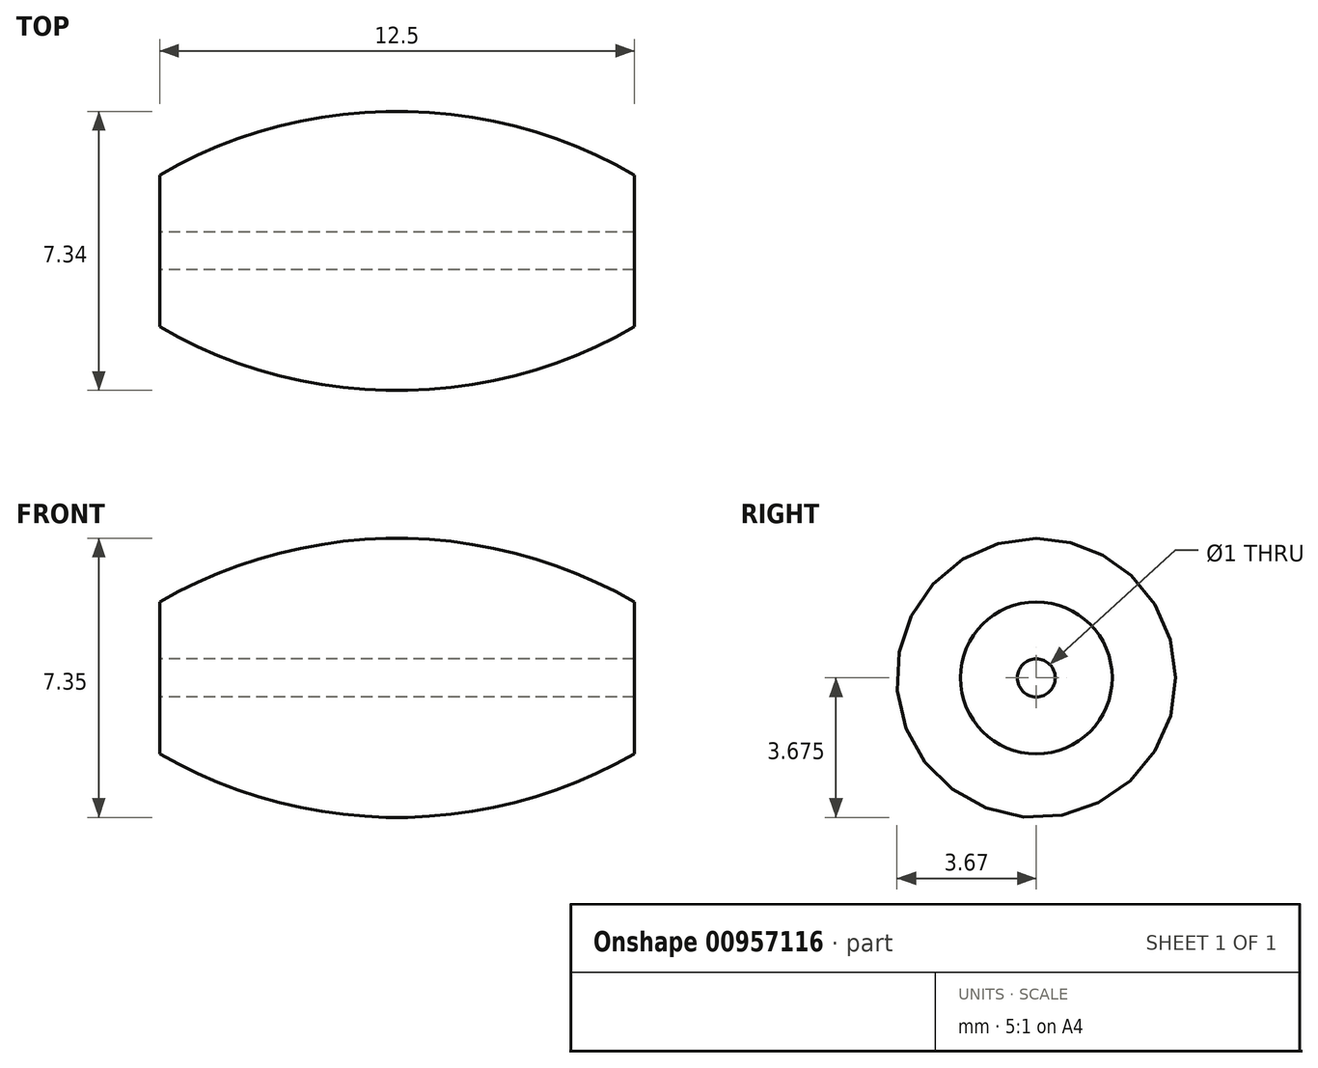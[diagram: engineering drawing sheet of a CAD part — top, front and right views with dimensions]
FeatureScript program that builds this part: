
annotation { "Feature Type Name" : "Feature", "Feature Type Description" : "" }
export const myFeature = defineFeature(function(context is Context, id is Id, definition is map)
    precondition{}
    {
        {
            var Q0;
            Q0=qCreatedBy(makeId("Front.planeOp"),FACE);
            var sketch = newSketch(context, id + "F0", { "sketchPlane" : qUnion([Q0])});
            skArc(sketch, "E0", {"start": v(6.25, 10.83) * mm, "mid": v(0, 12.5) * mm, "end": v(-6.25, 10.83) * mm});
            skLineSegment(sketch, "E1", {"start": v(0, 0) * mm, "end": v(0, 18.01) * mm, "construction": true});
            skLineSegment(sketch, "E2", {"start": v(0, 0) * mm, "end": v(-9.74, 16.86) * mm, "construction": true});
            skLineSegment(sketch, "E3", {"start": v(-6.25, 10.83) * mm, "end": v(-6.25, 9.33) * mm});
            skLineSegment(sketch, "E4", {"start": v(-6.25, 9.33) * mm, "end": v(0, 9.33) * mm});
            skLineSegment(sketch, "E5", {"start": v(-11.7, 8.83) * mm, "end": v(16.89, 8.83) * mm, "construction": true});
            skLineSegment(sketch, "E6.MirrorCS", {"start": v(0, 0) * mm, "end": v(9.74, 16.86) * mm, "construction": true});
            skLineSegment(sketch, "E7.MirrorCS", {"start": v(6.25, 9.33) * mm, "end": v(0, 9.33) * mm});
            skLineSegment(sketch, "E8.MirrorCS", {"start": v(6.25, 10.83) * mm, "end": v(6.25, 9.33) * mm});
            skSolve(sketch);
        }
        {
            var Q0;
            Q0 = qSketchRegion(id + "F0", true);
            var Q1;
            Q1=sQuery(id+"F0.wireOp",EDGE,"E5");
            revolve(context, id + "F1", {"surfaceOperationType" : NewSurfaceOperationType.NEW, "entities" : qUnion([Q0]), "axis" : qUnion([Q1]), "revolveType" : RevolveType.FULL});
        }
    });
